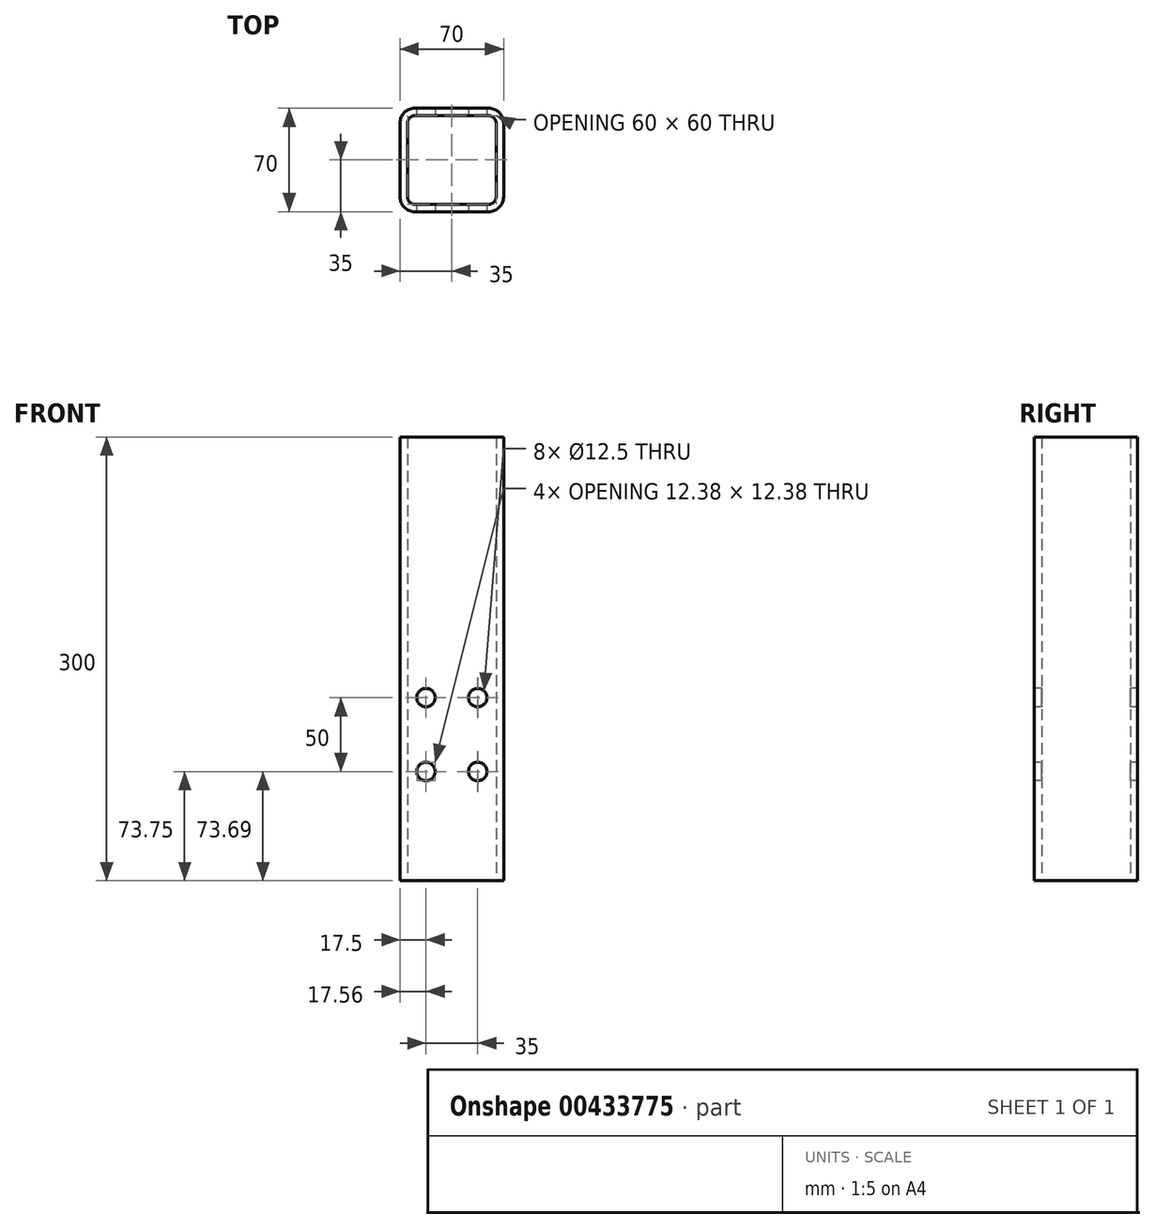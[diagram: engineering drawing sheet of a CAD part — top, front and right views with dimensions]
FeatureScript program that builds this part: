
annotation { "Feature Type Name" : "Feature", "Feature Type Description" : "" }
export const myFeature = defineFeature(function(context is Context, id is Id, definition is map)
    precondition{}
    {
        {
            var Q0;
            Q0=qCreatedBy(makeId("Top.planeOp"),FACE);
            var sketch = newSketch(context, id + "F0", { "sketchPlane" : qUnion([Q0])});
            skLineSegment(sketch, "E0.bottom", {"start": v(25, -35) * mm, "end": v(-25, -35) * mm});
            skLineSegment(sketch, "E0.top", {"start": v(25, 35) * mm, "end": v(-25, 35) * mm});
            skLineSegment(sketch, "E0.left", {"start": v(35, -25) * mm, "end": v(35, 25) * mm});
            skLineSegment(sketch, "E0.right", {"start": v(-35, -25) * mm, "end": v(-35, 25) * mm});
            skPoint(sketch, "E0.middle", {"position": v(0, 0) * mm});
            skPoint(sketch, "E1.visualSharp", {"position": v(35, -35) * mm});
            skArc(sketch, "E1.filletArc", {"start": v(25, -35) * mm, "mid": v(32.07, -32.07) * mm, "end": v(35, -25) * mm});
            skPoint(sketch, "E2.visualSharp", {"position": v(35, 35) * mm});
            skArc(sketch, "E2.filletArc", {"start": v(35, 25) * mm, "mid": v(32.07, 32.07) * mm, "end": v(25, 35) * mm});
            skPoint(sketch, "E3.visualSharp", {"position": v(-35, 35) * mm});
            skArc(sketch, "E3.filletArc", {"start": v(-25, 35) * mm, "mid": v(-32.07, 32.07) * mm, "end": v(-35, 25) * mm});
            skPoint(sketch, "E4.visualSharp", {"position": v(-35, -35) * mm});
            skArc(sketch, "E4.filletArc", {"start": v(-35, -25) * mm, "mid": v(-32.07, -32.07) * mm, "end": v(-25, -35) * mm});
            skArc(sketch, "E5.0", {"start": v(30, 25) * mm, "mid": v(28.54, 28.54) * mm, "end": v(25, 30) * mm});
            skLineSegment(sketch, "E5.1", {"start": v(30, -25) * mm, "end": v(30, 25) * mm});
            skLineSegment(sketch, "E5.2", {"start": v(25, 30) * mm, "end": v(-25, 30) * mm});
            skArc(sketch, "E5.3", {"start": v(25, -30) * mm, "mid": v(28.54, -28.54) * mm, "end": v(30, -25) * mm});
            skArc(sketch, "E5.4", {"start": v(-25, 30) * mm, "mid": v(-28.54, 28.54) * mm, "end": v(-30, 25) * mm});
            skLineSegment(sketch, "E5.5", {"start": v(-30, -25) * mm, "end": v(-30, 25) * mm});
            skArc(sketch, "E5.6", {"start": v(-30, -25) * mm, "mid": v(-28.54, -28.54) * mm, "end": v(-25, -30) * mm});
            skLineSegment(sketch, "E5.7", {"start": v(25, -30) * mm, "end": v(-25, -30) * mm});
            skSolve(sketch);
        }
        {
            var Q0;
            Q0 = qSketchRegion(id + "F0", true);
            extrude(context, id + "F1", {"entities" : qUnion([Q0]), "depth" : 300 * mm});
        }
        {
            var Q0;
            Q0=makeQuery(id+"F1.opExtrude","SWEPT_FACE",FACE,{"disambiguationData":[OSD([sQuery(id+"F0.wireOp",EDGE,"E0.bottom")])]});
            var sketch = newSketch(context, id + "F2", { "sketchPlane" : qUnion([Q0])});
            skCircle(sketch, "E6", {"center": v(-17.5, 123.75) * mm, "radius": 6.25 * mm});
            skLineSegment(sketch, "E7", {"start": v(0, 300) * mm, "end": v(0, 139.38) * mm, "construction": true});
            skPoint(sketch, "E7.endSnap0", {"position": v(0, 300) * mm});
            skCircle(sketch, "E8.0.1.0", {"center": v(-17.5, 73.75) * mm, "radius": 6.25 * mm});
            skLineSegment(sketch, "E8.direction1", {"start": v(-17.5, 123.75) * mm, "end": v(17.5, 123.75) * mm, "construction": true});
            skLineSegment(sketch, "E8.direction2", {"start": v(-17.5, 123.75) * mm, "end": v(-17.5, 73.75) * mm, "construction": true});
            skCircle(sketch, "E9.MirrorC", {"center": v(17.5, 73.75) * mm, "radius": 6.25 * mm});
            skCircle(sketch, "E10.MirrorC", {"center": v(17.5, 123.75) * mm, "radius": 6.25 * mm});
            skSolve(sketch);
        }
        {
            var Q0;
            Q0 = qSketchRegion(id + "F2", true);
            extrude(context, id + "F3", {"entities" : qUnion([Q0]), "operationType" : NewBodyOperationType.REMOVE, "endBound" : BoundingType.THROUGH_ALL, "oppositeDirection" : true, "depth" : 25 * mm});
        }
    });
